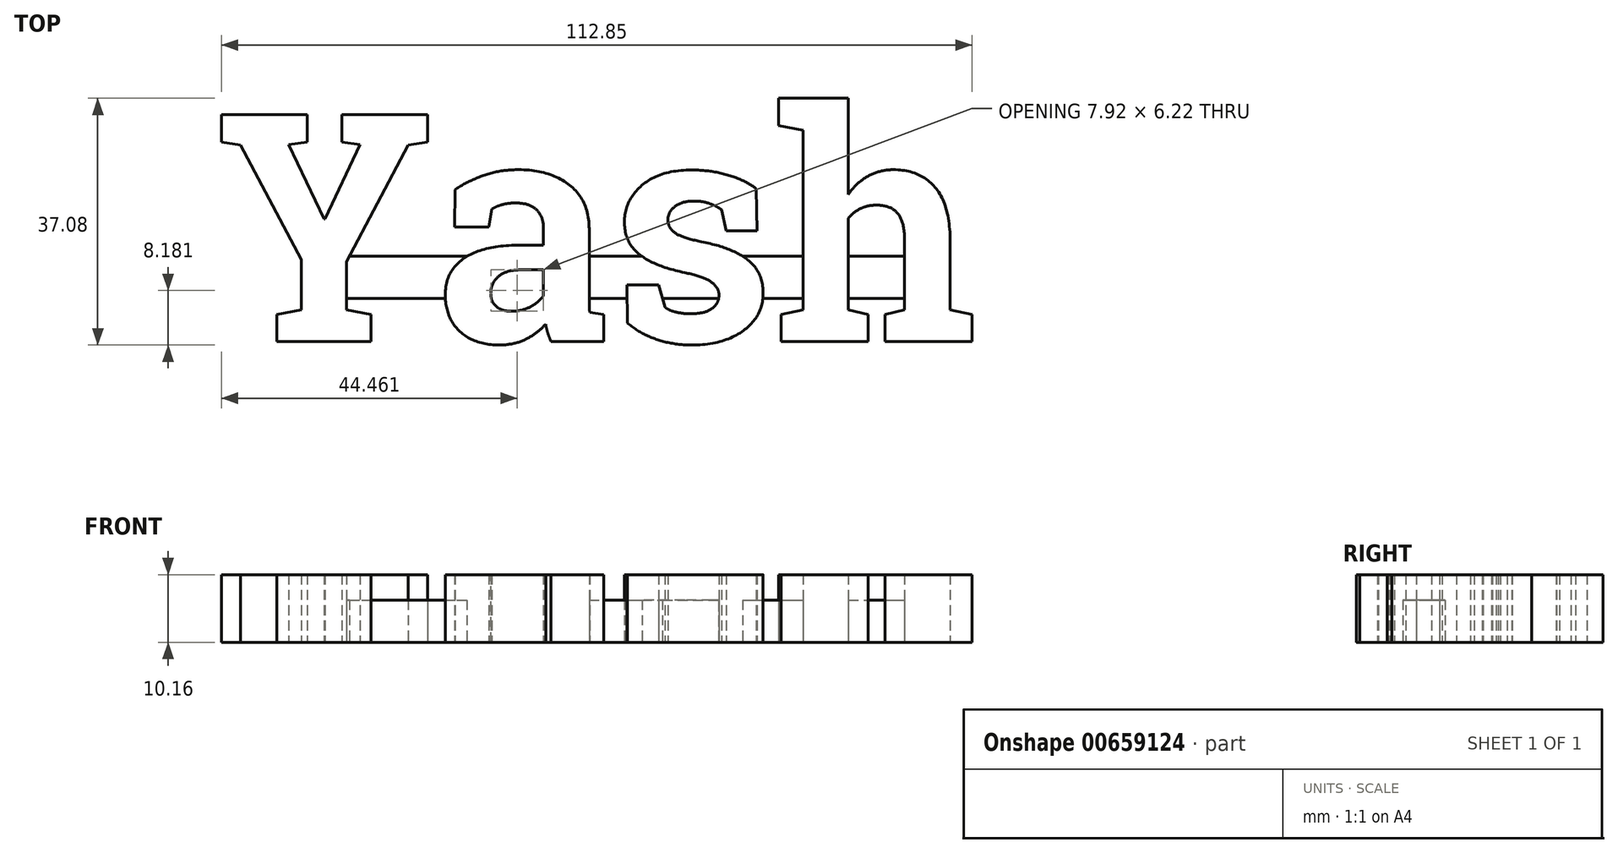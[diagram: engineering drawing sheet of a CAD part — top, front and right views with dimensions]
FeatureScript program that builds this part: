
annotation { "Feature Type Name" : "Feature", "Feature Type Description" : "" }
export const myFeature = defineFeature(function(context is Context, id is Id, definition is map)
    precondition{}
    {
        {
            var Q0;
            Q0=qCreatedBy(makeId("Top.planeOp"),FACE);
            var sketch = newSketch(context, id + "F0", { "sketchPlane" : qUnion([Q0])});
            skText(sketch, "E0", { "text": "Yash", "fontName": "RobotoSlab-Bold.ttf"});
            skLineSegment(sketch, "E1.bottom", {"start": v(15.39, -21.75) * mm, "end": v(107.96, -21.75) * mm});
            skLineSegment(sketch, "E1.top", {"start": v(15.39, -28.1) * mm, "end": v(107.96, -28.1) * mm});
            skLineSegment(sketch, "E1.left", {"start": v(15.39, -21.75) * mm, "end": v(15.39, -28.1) * mm});
            skLineSegment(sketch, "E1.right", {"start": v(107.96, -21.75) * mm, "end": v(107.96, -28.1) * mm});
            const initialGuessF0  = {"E0": [0, -0.03458, 1, 0, 0.03458]};
            skSetInitialGuess(sketch, initialGuessF0);
            skSolve(sketch);
        }
        {
            var Q0;
            Q0=makeQuery(id+"F0.imprint","IMPRINT",FACE,{"disambiguationData":[TD([[makeQuery(id+"F0.imprint","IMPRINT",EDGE,{"derivedFrom":sQuery(id+"F0.wireOp",EDGE,"E0.sketch_text.stroke-0")}),-1.0]])]});
            var Q1;
            {var subQ0=sQuery(id+"F0.wireOp",EDGE,"E1.left");Q1=makeQuery(id+"F0.imprint","IMPRINT",FACE,{"disambiguationData":[TD([[makeQuery(id+"F0.imprint","IMPRINT",EDGE,{"derivedFrom":subQ0}),1.0]])]});}
            var Q2;
            {var subQ0=sQuery(id+"F0.wireOp",EDGE,"E0.sketch_text.stroke-30");Q2=makeQuery(id+"F0.imprint","IMPRINT",FACE,{"disambiguationData":[TD([[makeQuery(id+"F0.imprint","IMPRINT",EDGE,{"derivedFrom":subQ0}),-1.0]])]});}
            var Q3;
            {var subQ7=sQuery(id+"F0.wireOp",EDGE,"E0.sketch_text.stroke-28");Q3=makeQuery(id+"F0.imprint","IMPRINT",FACE,{"disambiguationData":[TD([[makeQuery(id+"F0.imprint","IMPRINT",EDGE,{"derivedFrom":subQ7}),-1.0]])]});}
            var Q4;
            Q4=makeQuery(id+"F0.imprint","IMPRINT",FACE,{"disambiguationData":[TD([[makeQuery(id+"F0.imprint","IMPRINT",EDGE,{"derivedFrom":sQuery(id+"F0.wireOp",EDGE,"E0.sketch_text.stroke-22")}),-1.0]])]});
            var Q5;
            Q5=makeQuery(id+"F0.imprint","IMPRINT",FACE,{"disambiguationData":[TD([[makeQuery(id+"F0.imprint","IMPRINT",EDGE,{"derivedFrom":sQuery(id+"F0.wireOp",EDGE,"E0.sketch_text.stroke-57")}),-1.0]])]});
            var Q6;
            {var subQ1=sQuery(id+"F0.wireOp",EDGE,"E0.sketch_text.stroke-66");Q6=makeQuery(id+"F0.imprint","IMPRINT",FACE,{"disambiguationData":[TD([[makeQuery(id+"F0.imprint","IMPRINT",EDGE,{"derivedFrom":subQ1}),-1.0]])]});}
            var Q7;
            {var subQ12=sQuery(id+"F0.wireOp",EDGE,"E0.sketch_text.stroke-68");Q7=makeQuery(id+"F0.imprint","IMPRINT",FACE,{"disambiguationData":[TD([[makeQuery(id+"F0.imprint","IMPRINT",EDGE,{"derivedFrom":subQ12}),-1.0]])]});}
            var Q8;
            {var subQ0=sQuery(id+"F0.wireOp",EDGE,"E0.sketch_text.stroke-72");Q8=makeQuery(id+"F0.imprint","IMPRINT",FACE,{"disambiguationData":[TD([[makeQuery(id+"F0.imprint","IMPRINT",EDGE,{"derivedFrom":subQ0}),-1.0]])]});}
            var Q9;
            {var subQ11=sQuery(id+"F0.wireOp",EDGE,"E0.sketch_text.stroke-89");Q9=makeQuery(id+"F0.imprint","IMPRINT",FACE,{"disambiguationData":[TD([[makeQuery(id+"F0.imprint","IMPRINT",EDGE,{"derivedFrom":subQ11}),-1.0]])]});}
            var Q10;
            {var subQ0=sQuery(id+"F0.wireOp",EDGE,"E1.top");var subQ1=sQuery(id+"F0.wireOp",EDGE,"E0.sketch_text.stroke-88");var subQ2=makeQuery(id+"F0.imprint","INTERSECT",VERTEX,{"derivedFrom":[subQ1,subQ0]});Q10=makeQuery(id+"F0.imprint","IMPRINT",FACE,{"disambiguationData":[TD([[makeQuery(id+"F0.imprint","IMPRINT",EDGE,{"disambiguationData":[TD([[subQ2,-1.0]])],"derivedFrom":subQ1}),-1.0]])]});}
            var Q11;
            {var subQ5=sQuery(id+"F0.wireOp",EDGE,"E0.sketch_text.stroke-87");Q11=makeQuery(id+"F0.imprint","IMPRINT",FACE,{"disambiguationData":[TD([[makeQuery(id+"F0.imprint","IMPRINT",EDGE,{"derivedFrom":subQ5}),-1.0]])]});}
            var Q12;
            {var subQ5=sQuery(id+"F0.wireOp",EDGE,"E1.right");Q12=makeQuery(id+"F0.imprint","IMPRINT",FACE,{"disambiguationData":[TD([[makeQuery(id+"F0.imprint","IMPRINT",EDGE,{"derivedFrom":subQ5}),-1.0]])]});}
            extrude(context, id + "F1", {"entities" : qUnion([Q0, Q1, Q2, Q3, Q4, Q5, Q6, Q7, Q8, Q9, Q10, Q11, Q12]), "depth" : 10.16 * mm, "offsetDistance" : 25.4 * mm});
        }
        {
            var Q0;
            {var subQ0=sQuery(id+"F0.wireOp",EDGE,"E0.sketch_text.stroke-28");Q0=makeQuery(id+"F0.imprint","IMPRINT",FACE,{"disambiguationData":[TD([[makeQuery(id+"F0.imprint","IMPRINT",EDGE,{"derivedFrom":subQ0}),1.0]])]});}
            var Q1;
            {var subQ13=sQuery(id+"F0.wireOp",EDGE,"E0.sketch_text.stroke-72");Q1=makeQuery(id+"F0.imprint","IMPRINT",FACE,{"disambiguationData":[TD([[makeQuery(id+"F0.imprint","IMPRINT",EDGE,{"derivedFrom":subQ13}),1.0]])]});}
            var Q2;
            {var subQ0=sQuery(id+"F0.wireOp",EDGE,"E1.top");var subQ1=sQuery(id+"F0.wireOp",EDGE,"E0.sketch_text.stroke-103");var subQ2=makeQuery(id+"F0.imprint","INTERSECT",VERTEX,{"derivedFrom":[subQ1,subQ0]});Q2=makeQuery(id+"F0.imprint","IMPRINT",FACE,{"disambiguationData":[TD([[makeQuery(id+"F0.imprint","IMPRINT",EDGE,{"disambiguationData":[TD([[subQ2,-1.0]])],"derivedFrom":subQ1}),1.0]])]});}
            var Q3;
            {var subQ6=sQuery(id+"F0.wireOp",EDGE,"E0.sketch_text.stroke-66");Q3=makeQuery(id+"F0.imprint","IMPRINT",FACE,{"disambiguationData":[TD([[makeQuery(id+"F0.imprint","IMPRINT",EDGE,{"derivedFrom":subQ6}),1.0]])]});}
            extrude(context, id + "F2", {"entities" : qUnion([Q0, Q1, Q2, Q3]), "depth" : 6.35 * mm, "offsetDistance" : 25.4 * mm});
        }
    });
